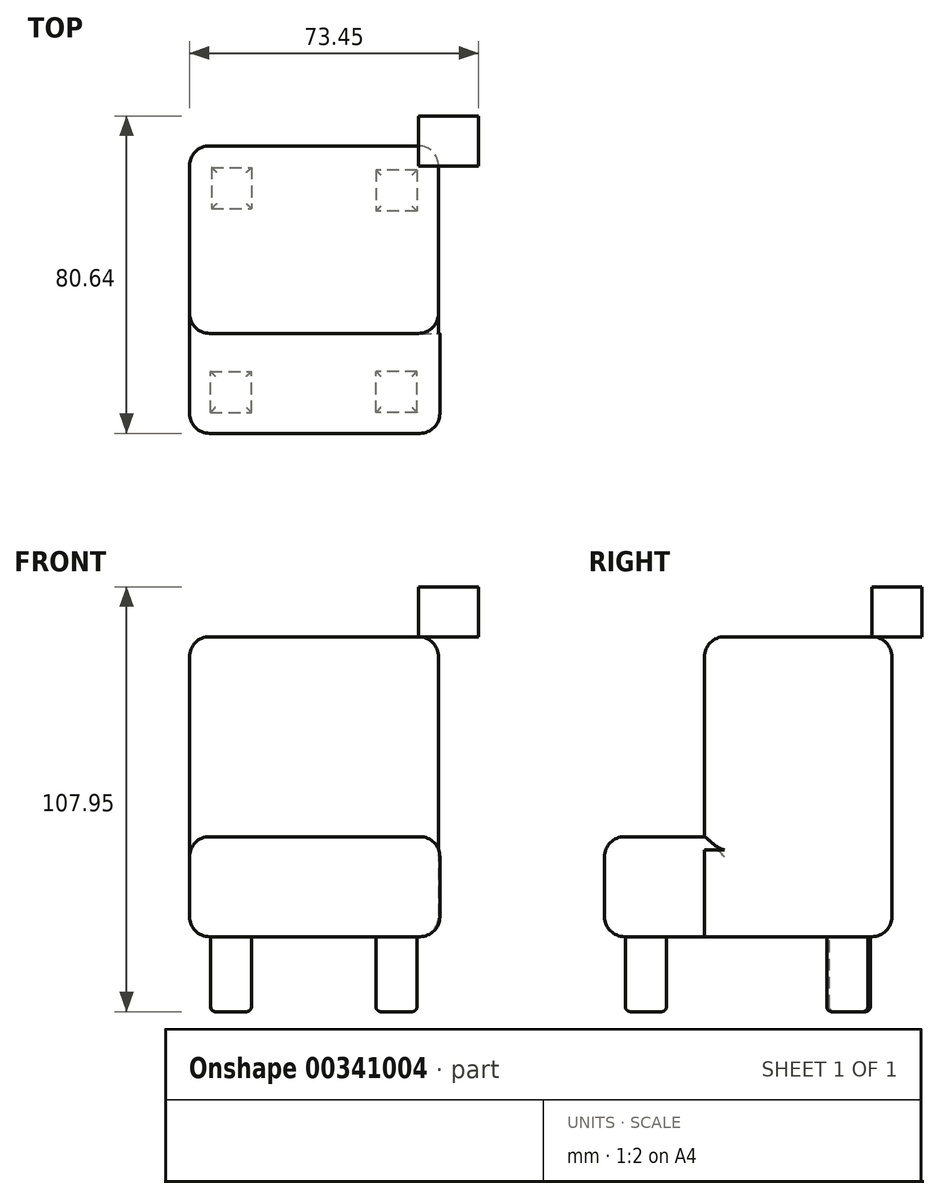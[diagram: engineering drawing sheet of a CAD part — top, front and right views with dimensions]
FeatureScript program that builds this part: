
annotation { "Feature Type Name" : "Feature", "Feature Type Description" : "" }
export const myFeature = defineFeature(function(context is Context, id is Id, definition is map)
    precondition{}
    {
        {
            var Q0;
            Q0=qCreatedBy(makeId("Front.planeOp"),FACE);
            var sketch = newSketch(context, id + "F0", { "sketchPlane" : qUnion([Q0])});
            skLineSegment(sketch, "E0.bottom", {"start": v(0, 0) * mm, "end": v(63.6, 0) * mm});
            skLineSegment(sketch, "E0.top", {"start": v(0, 25.4) * mm, "end": v(63.6, 25.4) * mm});
            skLineSegment(sketch, "E0.left", {"start": v(0, 0) * mm, "end": v(0, 25.4) * mm});
            skLineSegment(sketch, "E0.right", {"start": v(63.6, 0) * mm, "end": v(63.6, 25.4) * mm});
            skSolve(sketch);
        }
        {
            var Q0;
            Q0=makeQuery(id+"F0.imprint","IMPRINT",FACE,{"disambiguationData":[TD([[makeQuery(id+"F0.imprint","IMPRINT",EDGE,{"derivedFrom":sQuery(id+"F0.wireOp",EDGE,"E0.bottom")}),1.0]])]});
            extrude(context, id + "F1", {"entities" : qUnion([Q0]), "depth" : 25.4 * mm});
        }
        {
            var Q0;
            Q0=qCreatedBy(makeId("Top.planeOp"),FACE);
            var sketch = newSketch(context, id + "F2", { "sketchPlane" : qUnion([Q0])});
            skLineSegment(sketch, "E1.bottom", {"start": v(0, 0) * mm, "end": v(63.29, 0) * mm});
            skLineSegment(sketch, "E1.top", {"start": v(0, 47.62) * mm, "end": v(63.29, 47.62) * mm});
            skLineSegment(sketch, "E1.left", {"start": v(0, 0) * mm, "end": v(0, 47.62) * mm});
            skLineSegment(sketch, "E1.right", {"start": v(63.29, 0) * mm, "end": v(63.29, 47.62) * mm});
            skSolve(sketch);
        }
        {
            var Q0;
            Q0=makeQuery(id+"F2.imprint","IMPRINT",FACE,{"disambiguationData":[TD([[makeQuery(id+"F2.imprint","IMPRINT",EDGE,{"derivedFrom":sQuery(id+"F2.wireOp",EDGE,"E1.bottom")}),1.0]])]});
            extrude(context, id + "F3", {"entities" : qUnion([Q0]), "operationType" : NewBodyOperationType.ADD, "depth" : 76.2 * mm});
        }
        {
            var Q0;
            Q0=makeQuery(id+"F3.opExtrude","CAP_EDGE",EDGE,{"disambiguationData":[OSD([sQuery(id+"F2.wireOp",EDGE,"E1.right")])],"isStart":true});
            fillet(context, id + "F4", {"entities" : qUnion([Q0]), "radius" : 5.08 * mm, "tangentPropagation" : true, "allowEdgeOverflow" : false});
        }
        {
            var Q0;
            Q0=makeQuery(id+"F1.opExtrude","SWEPT_EDGE",EDGE,{"disambiguationData":[OSD([sQuery(id+"F0.wireOp",EDGE,"E0.bottom"),sQuery(id+"F0.wireOp",EDGE,"E0.right")])]});
            fillet(context, id + "F5", {"entities" : qUnion([Q0]), "radius" : 5.08 * mm, "tangentPropagation" : true, "allowEdgeOverflow" : false});
        }
        {
            var Q0;
            Q0=makeQuery(id+"F3.boolean.opBoolean","MERGE",EDGE,{"derivedFrom":[makeQuery(id+"F1.opExtrude","SWEPT_EDGE",EDGE,{"disambiguationData":[OSD([sQuery(id+"F0.wireOp",EDGE,"E0.bottom"),sQuery(id+"F0.wireOp",EDGE,"E0.left")])]}),makeQuery(id+"F3.opExtrude","CAP_EDGE",EDGE,{"disambiguationData":[OSD([sQuery(id+"F2.wireOp",EDGE,"E1.left")])],"isStart":true})]});
            fillet(context, id + "F6", {"entities" : qUnion([Q0]), "radius" : 5.08 * mm, "tangentPropagation" : true, "allowEdgeOverflow" : false});
        }
        {
            var Q0;
            Q0=makeQuery(id+"F1.opExtrude","SWEPT_EDGE",EDGE,{"disambiguationData":[OSD([sQuery(id+"F0.wireOp",EDGE,"E0.top"),sQuery(id+"F0.wireOp",EDGE,"E0.left")])]});
            var Q1;
            Q1=makeQuery(id+"F1.opExtrude","SWEPT_EDGE",EDGE,{"disambiguationData":[OSD([sQuery(id+"F0.wireOp",EDGE,"E0.top"),sQuery(id+"F0.wireOp",EDGE,"E0.right")])]});
            fillet(context, id + "F7", {"entities" : qUnion([Q0, Q1]), "radius" : 5.08 * mm, "tangentPropagation" : true, "allowEdgeOverflow" : false});
        }
        {
            var Q0;
            Q0=makeQuery(id+"F3.opExtrude","SWEPT_EDGE",EDGE,{"disambiguationData":[OSD([sQuery(id+"F2.wireOp",EDGE,"E1.bottom"),sQuery(id+"F2.wireOp",EDGE,"E1.left")])]});
            var Q1;
            {var subQ0=sQuery(id+"F2.wireOp",EDGE,"E1.right");var subQ2=sQuery(id+"F2.wireOp",EDGE,"E1.bottom");var subQ3=makeQuery(id+"F3.opExtrude","SWEPT_EDGE",EDGE,{"disambiguationData":[OSD([subQ2,subQ0])]});Q1=makeQuery(id+"F7.opFillet","MERGE",EDGE,{"derivedFrom":[makeQuery(id+"F3.boolean.opBoolean","SPLIT",EDGE,{"disambiguationData":[topologyDisambiguationEdgeConnected([makeQuery(id+"F3.opExtrude","SWEPT_FACE",FACE,{"disambiguationData":[OSD([subQ2])]})])],"derivedFrom":subQ3}),makeQuery(id+"F3.boolean.opBoolean","SPLIT",EDGE,{"disambiguationData":[topologyDisambiguationEdgeConnected([makeQuery(id+"F1.opExtrude","CAP_FACE",FACE,{"disambiguationData":[OSD([sQuery(id+"F0.wireOp",EDGE,"E0.bottom"),sQuery(id+"F0.wireOp",EDGE,"E0.top"),sQuery(id+"F0.wireOp",EDGE,"E0.left"),sQuery(id+"F0.wireOp",EDGE,"E0.right")])],"isStart":true})])],"derivedFrom":subQ3})]});}
            fillet(context, id + "F8", {"entities" : qUnion([Q0, Q1]), "radius" : 5.08 * mm, "tangentPropagation" : true, "allowEdgeOverflow" : false});
        }
        {
            var Q0;
            Q0=makeQuery(id+"F3.opExtrude","CAP_EDGE",EDGE,{"disambiguationData":[OSD([sQuery(id+"F2.wireOp",EDGE,"E1.right")])],"isStart":false});
            var Q1;
            Q1=makeQuery(id+"F3.opExtrude","CAP_EDGE",EDGE,{"disambiguationData":[OSD([sQuery(id+"F2.wireOp",EDGE,"E1.left")])],"isStart":false});
            fillet(context, id + "F9", {"entities" : qUnion([Q0, Q1]), "radius" : 5.08 * mm, "tangentPropagation" : true, "allowEdgeOverflow" : false});
        }
        {
            var Q0;
            Q0=makeQuery(id+"F3.opExtrude","CAP_EDGE",EDGE,{"disambiguationData":[OSD([sQuery(id+"F2.wireOp",EDGE,"E1.top")])],"isStart":false});
            fillet(context, id + "F10", {"entities" : qUnion([Q0]), "radius" : 5.08 * mm, "tangentPropagation" : true, "allowEdgeOverflow" : false});
        }
        {
            var Q0;
            Q0=makeQuery(id+"F1.opExtrude","CAP_EDGE",EDGE,{"disambiguationData":[OSD([sQuery(id+"F0.wireOp",EDGE,"E0.top")])],"isStart":false});
            fillet(context, id + "F11", {"entities" : qUnion([Q0]), "radius" : 5.08 * mm, "tangentPropagation" : true, "allowEdgeOverflow" : false});
        }
        {
            var Q0;
            Q0=qCreatedBy(makeId("Top.planeOp"),FACE);
            var sketch = newSketch(context, id + "F12", { "sketchPlane" : qUnion([Q0])});
            skLineSegment(sketch, "E2.bottom", {"start": v(5.32, -20.1) * mm, "end": v(15.75, -20.1) * mm});
            skLineSegment(sketch, "E2.top", {"start": v(5.32, -9.67) * mm, "end": v(15.75, -9.67) * mm});
            skLineSegment(sketch, "E2.left", {"start": v(5.32, -20.1) * mm, "end": v(5.32, -9.67) * mm});
            skLineSegment(sketch, "E2.right", {"start": v(15.75, -20.1) * mm, "end": v(15.75, -9.67) * mm});
            skLineSegment(sketch, "E3.bottom", {"start": v(57.8, -20.1) * mm, "end": v(47.37, -20.1) * mm});
            skLineSegment(sketch, "E3.top", {"start": v(57.8, -9.67) * mm, "end": v(47.37, -9.67) * mm});
            skLineSegment(sketch, "E3.left", {"start": v(57.8, -20.1) * mm, "end": v(57.8, -9.67) * mm});
            skLineSegment(sketch, "E3.right", {"start": v(47.37, -20.1) * mm, "end": v(47.37, -9.67) * mm});
            skLineSegment(sketch, "E4.bottom", {"start": v(57.8, 41.48) * mm, "end": v(47.37, 41.48) * mm});
            skLineSegment(sketch, "E4.top", {"start": v(57.8, 31.06) * mm, "end": v(47.37, 31.06) * mm});
            skLineSegment(sketch, "E4.left", {"start": v(57.8, 41.48) * mm, "end": v(57.8, 31.06) * mm});
            skLineSegment(sketch, "E4.right", {"start": v(47.37, 41.48) * mm, "end": v(47.37, 31.06) * mm});
            skLineSegment(sketch, "E5.bottom", {"start": v(5.64, 42.14) * mm, "end": v(15.75, 42.14) * mm});
            skLineSegment(sketch, "E5.top", {"start": v(5.64, 31.71) * mm, "end": v(15.75, 31.71) * mm});
            skLineSegment(sketch, "E5.left", {"start": v(5.64, 42.14) * mm, "end": v(5.64, 31.71) * mm});
            skLineSegment(sketch, "E5.right", {"start": v(15.75, 42.14) * mm, "end": v(15.75, 31.71) * mm});
            skSolve(sketch);
        }
        {
            var Q0;
            Q0=makeQuery(id+"F12.imprint","IMPRINT",FACE,{"disambiguationData":[TD([[makeQuery(id+"F12.imprint","IMPRINT",EDGE,{"derivedFrom":sQuery(id+"F12.wireOp",EDGE,"E3.bottom")}),-1.0]])]});
            var Q1;
            Q1=makeQuery(id+"F12.imprint","IMPRINT",FACE,{"disambiguationData":[TD([[makeQuery(id+"F12.imprint","IMPRINT",EDGE,{"derivedFrom":sQuery(id+"F12.wireOp",EDGE,"E2.bottom")}),1.0]])]});
            var Q2;
            Q2=makeQuery(id+"F12.imprint","IMPRINT",FACE,{"disambiguationData":[TD([[makeQuery(id+"F12.imprint","IMPRINT",EDGE,{"derivedFrom":sQuery(id+"F12.wireOp",EDGE,"E4.bottom")}),1.0]])]});
            var Q3;
            Q3=makeQuery(id+"F12.imprint","IMPRINT",FACE,{"disambiguationData":[TD([[makeQuery(id+"F12.imprint","IMPRINT",EDGE,{"derivedFrom":sQuery(id+"F12.wireOp",EDGE,"E5.bottom")}),-1.0]])]});
            extrude(context, id + "F13", {"entities" : qUnion([Q0, Q1, Q2, Q3]), "operationType" : NewBodyOperationType.ADD, "oppositeDirection" : true, "depth" : 19.05 * mm});
        }
        {
            var Q0;
            Q0=makeQuery(id+"F13.opExtrude","CAP_EDGE",EDGE,{"disambiguationData":[OSD([sQuery(id+"F12.wireOp",EDGE,"E4.left")])],"isStart":false});
            var Q1;
            Q1=makeQuery(id+"F13.opExtrude","CAP_EDGE",EDGE,{"disambiguationData":[OSD([sQuery(id+"F12.wireOp",EDGE,"E4.top")])],"isStart":false});
            var Q2;
            Q2=makeQuery(id+"F13.opExtrude","CAP_EDGE",EDGE,{"disambiguationData":[OSD([sQuery(id+"F12.wireOp",EDGE,"E4.bottom")])],"isStart":false});
            var Q3;
            Q3=makeQuery(id+"F13.opExtrude","CAP_EDGE",EDGE,{"disambiguationData":[OSD([sQuery(id+"F12.wireOp",EDGE,"E4.right")])],"isStart":false});
            fillet(context, id + "F14", {"entities" : qUnion([Q0, Q1, Q2, Q3]), "radius" : 1.27 * mm, "tangentPropagation" : true, "allowEdgeOverflow" : false});
        }
        {
            var Q0;
            Q0=makeQuery(id+"F13.opExtrude","CAP_EDGE",EDGE,{"disambiguationData":[OSD([sQuery(id+"F12.wireOp",EDGE,"E5.right")])],"isStart":false});
            var Q1;
            Q1=makeQuery(id+"F13.opExtrude","CAP_EDGE",EDGE,{"disambiguationData":[OSD([sQuery(id+"F12.wireOp",EDGE,"E5.top")])],"isStart":false});
            var Q2;
            Q2=makeQuery(id+"F13.opExtrude","CAP_EDGE",EDGE,{"disambiguationData":[OSD([sQuery(id+"F12.wireOp",EDGE,"E5.bottom")])],"isStart":false});
            var Q3;
            Q3=makeQuery(id+"F13.opExtrude","CAP_EDGE",EDGE,{"disambiguationData":[OSD([sQuery(id+"F12.wireOp",EDGE,"E5.left")])],"isStart":false});
            fillet(context, id + "F15", {"entities" : qUnion([Q0, Q1, Q2, Q3]), "radius" : 1.27 * mm, "tangentPropagation" : true, "allowEdgeOverflow" : false});
        }
        {
            var Q0;
            Q0=makeQuery(id+"F13.opExtrude","CAP_EDGE",EDGE,{"disambiguationData":[OSD([sQuery(id+"F12.wireOp",EDGE,"E3.left")])],"isStart":false});
            var Q1;
            Q1=makeQuery(id+"F13.opExtrude","CAP_EDGE",EDGE,{"disambiguationData":[OSD([sQuery(id+"F12.wireOp",EDGE,"E3.top")])],"isStart":false});
            var Q2;
            Q2=makeQuery(id+"F13.opExtrude","CAP_EDGE",EDGE,{"disambiguationData":[OSD([sQuery(id+"F12.wireOp",EDGE,"E3.right")])],"isStart":false});
            var Q3;
            Q3=makeQuery(id+"F13.opExtrude","CAP_EDGE",EDGE,{"disambiguationData":[OSD([sQuery(id+"F12.wireOp",EDGE,"E3.bottom")])],"isStart":false});
            fillet(context, id + "F16", {"entities" : qUnion([Q0, Q1, Q2, Q3]), "radius" : 1.27 * mm, "tangentPropagation" : true, "allowEdgeOverflow" : false});
        }
        {
            var Q0;
            Q0=makeQuery(id+"F13.opExtrude","CAP_EDGE",EDGE,{"disambiguationData":[OSD([sQuery(id+"F12.wireOp",EDGE,"E2.right")])],"isStart":false});
            var Q1;
            Q1=makeQuery(id+"F13.opExtrude","CAP_EDGE",EDGE,{"disambiguationData":[OSD([sQuery(id+"F12.wireOp",EDGE,"E2.bottom")])],"isStart":false});
            var Q2;
            Q2=makeQuery(id+"F13.opExtrude","CAP_EDGE",EDGE,{"disambiguationData":[OSD([sQuery(id+"F12.wireOp",EDGE,"E2.left")])],"isStart":false});
            var Q3;
            Q3=makeQuery(id+"F13.opExtrude","CAP_EDGE",EDGE,{"disambiguationData":[OSD([sQuery(id+"F12.wireOp",EDGE,"E2.top")])],"isStart":false});
            fillet(context, id + "F17", {"entities" : qUnion([Q0, Q1, Q2, Q3]), "radius" : 1.27 * mm, "tangentPropagation" : true, "allowEdgeOverflow" : false});
        }
        {
            var Q0;
            Q0=makeQuery(id+"F3.opExtrude","CAP_FACE",FACE,{"disambiguationData":[OSD([sQuery(id+"F2.wireOp",EDGE,"E1.bottom"),sQuery(id+"F2.wireOp",EDGE,"E1.top"),sQuery(id+"F2.wireOp",EDGE,"E1.left"),sQuery(id+"F2.wireOp",EDGE,"E1.right")])],"isStart":false});
            var sketch = newSketch(context, id + "F18", { "sketchPlane" : qUnion([Q0])});
            skLineSegment(sketch, "E6.bottom", {"start": v(5.08, 42.54) * mm, "end": v(-10.16, 42.54) * mm});
            skLineSegment(sketch, "E6.top", {"start": v(5.08, 55.24) * mm, "end": v(-10.16, 55.24) * mm});
            skLineSegment(sketch, "E6.left", {"start": v(5.08, 42.54) * mm, "end": v(5.08, 55.24) * mm});
            skLineSegment(sketch, "E6.right", {"start": v(-10.16, 42.54) * mm, "end": v(-10.16, 55.24) * mm});
            skLineSegment(sketch, "E7.bottom", {"start": v(58.2, 42.54) * mm, "end": v(73.45, 42.54) * mm});
            skLineSegment(sketch, "E7.top", {"start": v(58.2, 55.24) * mm, "end": v(73.45, 55.24) * mm});
            skLineSegment(sketch, "E7.left", {"start": v(58.2, 42.54) * mm, "end": v(58.2, 55.24) * mm});
            skLineSegment(sketch, "E7.right", {"start": v(73.45, 42.54) * mm, "end": v(73.45, 55.24) * mm});
            skSolve(sketch);
        }
        {
            var Q0;
            Q0=makeQuery(id+"F18.imprint","IMPRINT",FACE,{"disambiguationData":[TD([[makeQuery(id+"F18.imprint","IMPRINT",EDGE,{"derivedFrom":sQuery(id+"F18.wireOp",EDGE,"E6.bottom")}),-1.0]])]});
            var Q1;
            Q1=makeQuery(id+"F18.imprint","IMPRINT",FACE,{"disambiguationData":[TD([[makeQuery(id+"F18.imprint","IMPRINT",EDGE,{"derivedFrom":sQuery(id+"F18.wireOp",EDGE,"E7.bottom")}),1.0]])]});
            extrude(context, id + "F19", {"entities" : qUnion([Q0, Q1]), "depth" : 12.7 * mm});
        }
        {
            var Q0;
            Q0=makeQuery(id+"F19.opExtrude","SWEPT_BODY",BODY,{"disambiguationData":[OSD([sQuery(id+"F18.wireOp",EDGE,"E6.bottom"),sQuery(id+"F18.wireOp",EDGE,"E6.top"),sQuery(id+"F18.wireOp",EDGE,"E6.left"),sQuery(id+"F18.wireOp",EDGE,"E6.right")])]});
            deleteBodies(context, id + "F20", {"entities" : qUnion([Q0])});
        }
    });
